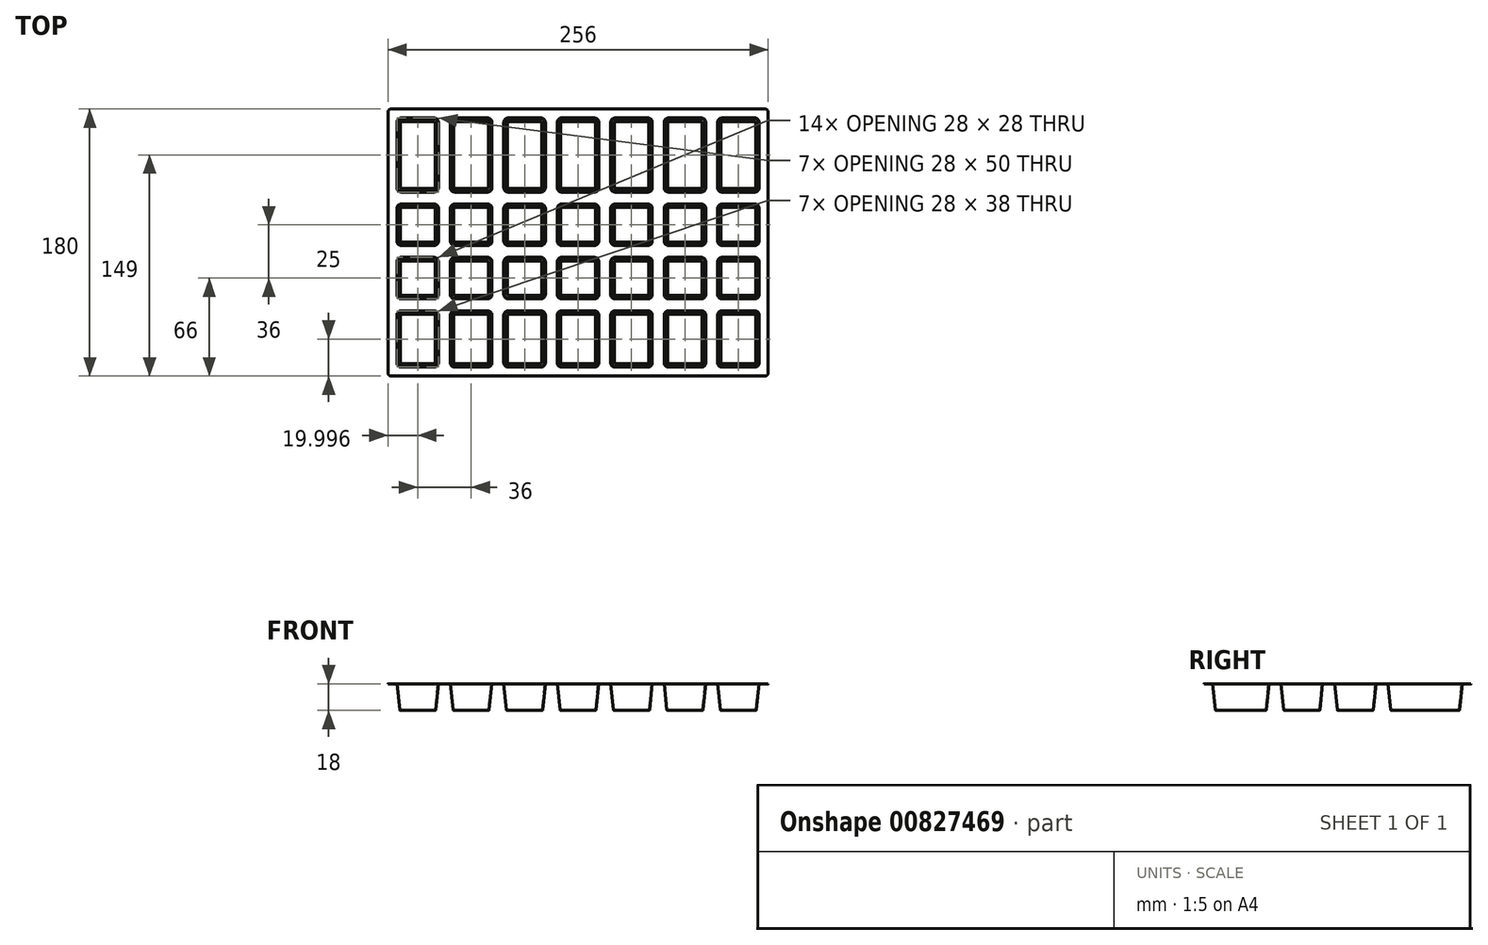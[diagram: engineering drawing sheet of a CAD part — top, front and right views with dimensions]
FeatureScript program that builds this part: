
annotation { "Feature Type Name" : "Feature", "Feature Type Description" : "" }
export const myFeature = defineFeature(function(context is Context, id is Id, definition is map)
    precondition{}
    {
        {
            var Q0;
            Q0=qCreatedBy(makeId("Top.planeOp"),FACE);
            var sketch = newSketch(context, id + "F0", { "sketchPlane" : qUnion([Q0])});
            skLineSegment(sketch, "E0.bottom", {"start": v(4.65, 0) * mm, "end": v(4.65, -180) * mm, "construction": true});
            skLineSegment(sketch, "E0.top", {"start": v(260.65, 0) * mm, "end": v(260.65, -180) * mm, "construction": true});
            skLineSegment(sketch, "E0.left", {"start": v(4.65, 0) * mm, "end": v(260.65, 0) * mm, "construction": true});
            skLineSegment(sketch, "E0.right", {"start": v(4.65, -180) * mm, "end": v(260.65, -180) * mm, "construction": true});
            skLineSegment(sketch, "E1", {"start": v(132.65, 0) * mm, "end": v(132.65, -180) * mm, "construction": true});
            skLineSegment(sketch, "E2.bottom", {"start": v(118.65, -9) * mm, "end": v(118.65, -53) * mm});
            skLineSegment(sketch, "E2.top", {"start": v(146.65, -9) * mm, "end": v(146.65, -53) * mm});
            skLineSegment(sketch, "E2.left", {"start": v(143.65, -6) * mm, "end": v(121.65, -6) * mm});
            skLineSegment(sketch, "E2.right", {"start": v(143.65, -56) * mm, "end": v(121.65, -56) * mm});
            skPoint(sketch, "E3", {"position": v(132.65, -6) * mm});
            skPoint(sketch, "E4.visualSharp", {"position": v(146.65, -6) * mm});
            skArc(sketch, "E4.filletArc", {"start": v(146.65, -9) * mm, "mid": v(145.77, -6.88) * mm, "end": v(143.65, -6) * mm});
            skPoint(sketch, "E5.visualSharp", {"position": v(118.65, -6) * mm});
            skArc(sketch, "E5.filletArc", {"start": v(121.65, -6) * mm, "mid": v(119.52, -6.88) * mm, "end": v(118.65, -9) * mm});
            skPoint(sketch, "E6.visualSharp", {"position": v(118.65, -56) * mm});
            skArc(sketch, "E6.filletArc", {"start": v(118.65, -53) * mm, "mid": v(119.52, -55.12) * mm, "end": v(121.65, -56) * mm});
            skPoint(sketch, "E7.visualSharp", {"position": v(146.65, -56) * mm});
            skArc(sketch, "E7.filletArc", {"start": v(143.65, -56) * mm, "mid": v(145.77, -55.12) * mm, "end": v(146.65, -53) * mm});
            skLineSegment(sketch, "E8.bottom", {"start": v(146.65, -67) * mm, "end": v(146.65, -89) * mm});
            skLineSegment(sketch, "E8.top", {"start": v(118.65, -67) * mm, "end": v(118.65, -89) * mm});
            skLineSegment(sketch, "E8.left", {"start": v(143.65, -64) * mm, "end": v(121.65, -64) * mm});
            skLineSegment(sketch, "E8.right", {"start": v(143.65, -92) * mm, "end": v(121.65, -92) * mm});
            skLineSegment(sketch, "E9.bottom", {"start": v(146.65, -103) * mm, "end": v(146.65, -125) * mm});
            skLineSegment(sketch, "E9.top", {"start": v(118.65, -103) * mm, "end": v(118.65, -125) * mm});
            skLineSegment(sketch, "E9.left", {"start": v(143.65, -100) * mm, "end": v(121.65, -100) * mm});
            skLineSegment(sketch, "E9.right", {"start": v(143.65, -128) * mm, "end": v(121.65, -128) * mm});
            skLineSegment(sketch, "E10.bottom", {"start": v(146.65, -139) * mm, "end": v(146.65, -171) * mm});
            skLineSegment(sketch, "E10.top", {"start": v(118.65, -139) * mm, "end": v(118.65, -171) * mm});
            skLineSegment(sketch, "E10.left", {"start": v(143.65, -136) * mm, "end": v(121.65, -136) * mm});
            skLineSegment(sketch, "E10.right", {"start": v(143.65, -174) * mm, "end": v(121.65, -174) * mm});
            skPoint(sketch, "E11.visualSharp", {"position": v(146.65, -64) * mm});
            skArc(sketch, "E11.filletArc", {"start": v(146.65, -67) * mm, "mid": v(145.77, -64.88) * mm, "end": v(143.65, -64) * mm});
            skPoint(sketch, "E12.visualSharp", {"position": v(146.65, -92) * mm});
            skArc(sketch, "E12.filletArc", {"start": v(143.65, -92) * mm, "mid": v(145.77, -91.12) * mm, "end": v(146.65, -89) * mm});
            skPoint(sketch, "E13.visualSharp", {"position": v(118.65, -92) * mm});
            skArc(sketch, "E13.filletArc", {"start": v(118.65, -89) * mm, "mid": v(119.52, -91.12) * mm, "end": v(121.65, -92) * mm});
            skPoint(sketch, "E14.visualSharp", {"position": v(118.65, -64) * mm});
            skArc(sketch, "E14.filletArc", {"start": v(121.65, -64) * mm, "mid": v(119.52, -64.88) * mm, "end": v(118.65, -67) * mm});
            skPoint(sketch, "E15.visualSharp", {"position": v(146.65, -100) * mm});
            skArc(sketch, "E15.filletArc", {"start": v(146.65, -103) * mm, "mid": v(145.77, -100.88) * mm, "end": v(143.65, -100) * mm});
            skPoint(sketch, "E16.visualSharp", {"position": v(146.65, -128) * mm});
            skArc(sketch, "E16.filletArc", {"start": v(143.65, -128) * mm, "mid": v(145.77, -127.12) * mm, "end": v(146.65, -125) * mm});
            skPoint(sketch, "E17.visualSharp", {"position": v(118.65, -128) * mm});
            skArc(sketch, "E17.filletArc", {"start": v(118.65, -125) * mm, "mid": v(119.52, -127.12) * mm, "end": v(121.65, -128) * mm});
            skPoint(sketch, "E18.visualSharp", {"position": v(118.65, -100) * mm});
            skArc(sketch, "E18.filletArc", {"start": v(121.65, -100) * mm, "mid": v(119.52, -100.88) * mm, "end": v(118.65, -103) * mm});
            skPoint(sketch, "E19.visualSharp", {"position": v(146.65, -136) * mm});
            skArc(sketch, "E19.filletArc", {"start": v(146.65, -139) * mm, "mid": v(145.77, -136.88) * mm, "end": v(143.65, -136) * mm});
            skPoint(sketch, "E20.visualSharp", {"position": v(146.65, -174) * mm});
            skArc(sketch, "E20.filletArc", {"start": v(143.65, -174) * mm, "mid": v(145.77, -173.12) * mm, "end": v(146.65, -171) * mm});
            skPoint(sketch, "E21.visualSharp", {"position": v(118.65, -174) * mm});
            skArc(sketch, "E21.filletArc", {"start": v(118.65, -171) * mm, "mid": v(119.52, -173.12) * mm, "end": v(121.65, -174) * mm});
            skPoint(sketch, "E22.visualSharp", {"position": v(118.65, -136) * mm});
            skArc(sketch, "E22.filletArc", {"start": v(121.65, -136) * mm, "mid": v(119.52, -136.88) * mm, "end": v(118.65, -139) * mm});
            skPoint(sketch, "E23.0.1.0", {"position": v(154.65, -56) * mm});
            skPoint(sketch, "E23.0.1.1", {"position": v(182.65, -56) * mm});
            skLineSegment(sketch, "E23.0.1.2", {"start": v(168.65, 0) * mm, "end": v(168.65, -180) * mm, "construction": true});
            skPoint(sketch, "E23.0.1.3", {"position": v(154.65, -6) * mm});
            skLineSegment(sketch, "E23.0.1.4", {"start": v(154.65, -9) * mm, "end": v(154.65, -53) * mm});
            skPoint(sketch, "E23.0.1.5", {"position": v(168.65, -6) * mm});
            skPoint(sketch, "E23.0.1.6", {"position": v(182.65, -174) * mm});
            skLineSegment(sketch, "E23.0.1.7", {"start": v(182.65, -67) * mm, "end": v(182.65, -89) * mm});
            skLineSegment(sketch, "E23.0.1.8", {"start": v(182.65, -9) * mm, "end": v(182.65, -53) * mm});
            skPoint(sketch, "E23.0.1.9", {"position": v(182.65, -64) * mm});
            skPoint(sketch, "E23.0.1.10", {"position": v(154.65, -174) * mm});
            skLineSegment(sketch, "E23.0.1.11", {"start": v(179.65, -64) * mm, "end": v(157.65, -64) * mm});
            skLineSegment(sketch, "E23.0.1.12", {"start": v(154.65, -139) * mm, "end": v(154.65, -171) * mm});
            skLineSegment(sketch, "E23.0.1.13", {"start": v(182.65, -103) * mm, "end": v(182.65, -125) * mm});
            skLineSegment(sketch, "E23.0.1.14", {"start": v(154.65, -103) * mm, "end": v(154.65, -125) * mm});
            skLineSegment(sketch, "E23.0.1.15", {"start": v(179.65, -174) * mm, "end": v(157.65, -174) * mm});
            skLineSegment(sketch, "E23.0.1.16", {"start": v(179.65, -92) * mm, "end": v(157.65, -92) * mm});
            skLineSegment(sketch, "E23.0.1.17", {"start": v(179.65, -56) * mm, "end": v(157.65, -56) * mm});
            skPoint(sketch, "E23.0.1.18", {"position": v(154.65, -92) * mm});
            skLineSegment(sketch, "E23.0.1.19", {"start": v(154.65, -67) * mm, "end": v(154.65, -89) * mm});
            skPoint(sketch, "E23.0.1.20", {"position": v(182.65, -128) * mm});
            skPoint(sketch, "E23.0.1.21", {"position": v(182.65, -136) * mm});
            skLineSegment(sketch, "E23.0.1.22", {"start": v(179.65, -100) * mm, "end": v(157.65, -100) * mm});
            skPoint(sketch, "E23.0.1.23", {"position": v(182.65, -100) * mm});
            skPoint(sketch, "E23.0.1.24", {"position": v(154.65, -64) * mm});
            skPoint(sketch, "E23.0.1.25", {"position": v(154.65, -128) * mm});
            skLineSegment(sketch, "E23.0.1.26", {"start": v(179.65, -128) * mm, "end": v(157.65, -128) * mm});
            skPoint(sketch, "E23.0.1.27", {"position": v(154.65, -100) * mm});
            skLineSegment(sketch, "E23.0.1.28", {"start": v(182.65, -139) * mm, "end": v(182.65, -171) * mm});
            skPoint(sketch, "E23.0.1.29", {"position": v(182.65, -92) * mm});
            skLineSegment(sketch, "E23.0.1.30", {"start": v(179.65, -6) * mm, "end": v(157.65, -6) * mm});
            skPoint(sketch, "E23.0.1.31", {"position": v(182.65, -6) * mm});
            skPoint(sketch, "E23.0.1.32", {"position": v(154.65, -136) * mm});
            skLineSegment(sketch, "E23.0.1.33", {"start": v(179.65, -136) * mm, "end": v(157.65, -136) * mm});
            skArc(sketch, "E23.0.1.34", {"start": v(154.65, -89) * mm, "mid": v(155.52, -91.12) * mm, "end": v(157.65, -92) * mm});
            skArc(sketch, "E23.0.1.35", {"start": v(154.65, -53) * mm, "mid": v(155.52, -55.12) * mm, "end": v(157.65, -56) * mm});
            skArc(sketch, "E23.0.1.36", {"start": v(182.65, -139) * mm, "mid": v(181.77, -136.88) * mm, "end": v(179.65, -136) * mm});
            skArc(sketch, "E23.0.1.37", {"start": v(157.65, -64) * mm, "mid": v(155.52, -64.88) * mm, "end": v(154.65, -67) * mm});
            skArc(sketch, "E23.0.1.38", {"start": v(179.65, -56) * mm, "mid": v(181.77, -55.12) * mm, "end": v(182.65, -53) * mm});
            skArc(sketch, "E23.0.1.39", {"start": v(154.65, -171) * mm, "mid": v(155.52, -173.12) * mm, "end": v(157.65, -174) * mm});
            skArc(sketch, "E23.0.1.40", {"start": v(157.65, -6) * mm, "mid": v(155.52, -6.88) * mm, "end": v(154.65, -9) * mm});
            skArc(sketch, "E23.0.1.41", {"start": v(157.65, -136) * mm, "mid": v(155.52, -136.88) * mm, "end": v(154.65, -139) * mm});
            skArc(sketch, "E23.0.1.42", {"start": v(157.65, -100) * mm, "mid": v(155.52, -100.88) * mm, "end": v(154.65, -103) * mm});
            skArc(sketch, "E23.0.1.43", {"start": v(182.65, -67) * mm, "mid": v(181.77, -64.88) * mm, "end": v(179.65, -64) * mm});
            skArc(sketch, "E23.0.1.44", {"start": v(154.65, -125) * mm, "mid": v(155.52, -127.12) * mm, "end": v(157.65, -128) * mm});
            skArc(sketch, "E23.0.1.45", {"start": v(179.65, -128) * mm, "mid": v(181.77, -127.12) * mm, "end": v(182.65, -125) * mm});
            skArc(sketch, "E23.0.1.46", {"start": v(179.65, -92) * mm, "mid": v(181.77, -91.12) * mm, "end": v(182.65, -89) * mm});
            skArc(sketch, "E23.0.1.47", {"start": v(182.65, -103) * mm, "mid": v(181.77, -100.88) * mm, "end": v(179.65, -100) * mm});
            skArc(sketch, "E23.0.1.48", {"start": v(179.65, -174) * mm, "mid": v(181.77, -173.12) * mm, "end": v(182.65, -171) * mm});
            skArc(sketch, "E23.0.1.49", {"start": v(182.65, -9) * mm, "mid": v(181.77, -6.88) * mm, "end": v(179.65, -6) * mm});
            skPoint(sketch, "E23.0.2.0", {"position": v(190.65, -56) * mm});
            skPoint(sketch, "E23.0.2.1", {"position": v(218.65, -56) * mm});
            skLineSegment(sketch, "E23.0.2.2", {"start": v(204.65, 0) * mm, "end": v(204.65, -180) * mm, "construction": true});
            skPoint(sketch, "E23.0.2.3", {"position": v(190.65, -6) * mm});
            skLineSegment(sketch, "E23.0.2.4", {"start": v(190.65, -9) * mm, "end": v(190.65, -53) * mm});
            skPoint(sketch, "E23.0.2.5", {"position": v(204.65, -6) * mm});
            skPoint(sketch, "E23.0.2.6", {"position": v(218.65, -174) * mm});
            skLineSegment(sketch, "E23.0.2.7", {"start": v(218.65, -67) * mm, "end": v(218.65, -89) * mm});
            skLineSegment(sketch, "E23.0.2.8", {"start": v(218.65, -9) * mm, "end": v(218.65, -53) * mm});
            skPoint(sketch, "E23.0.2.9", {"position": v(218.65, -64) * mm});
            skPoint(sketch, "E23.0.2.10", {"position": v(190.65, -174) * mm});
            skLineSegment(sketch, "E23.0.2.11", {"start": v(215.65, -64) * mm, "end": v(193.65, -64) * mm});
            skLineSegment(sketch, "E23.0.2.12", {"start": v(190.65, -139) * mm, "end": v(190.65, -171) * mm});
            skLineSegment(sketch, "E23.0.2.13", {"start": v(218.65, -103) * mm, "end": v(218.65, -125) * mm});
            skLineSegment(sketch, "E23.0.2.14", {"start": v(190.65, -103) * mm, "end": v(190.65, -125) * mm});
            skLineSegment(sketch, "E23.0.2.15", {"start": v(215.65, -174) * mm, "end": v(193.65, -174) * mm});
            skLineSegment(sketch, "E23.0.2.16", {"start": v(215.65, -92) * mm, "end": v(193.65, -92) * mm});
            skLineSegment(sketch, "E23.0.2.17", {"start": v(215.65, -56) * mm, "end": v(193.65, -56) * mm});
            skPoint(sketch, "E23.0.2.18", {"position": v(190.65, -92) * mm});
            skLineSegment(sketch, "E23.0.2.19", {"start": v(190.65, -67) * mm, "end": v(190.65, -89) * mm});
            skPoint(sketch, "E23.0.2.20", {"position": v(218.65, -128) * mm});
            skPoint(sketch, "E23.0.2.21", {"position": v(218.65, -136) * mm});
            skLineSegment(sketch, "E23.0.2.22", {"start": v(215.65, -100) * mm, "end": v(193.65, -100) * mm});
            skPoint(sketch, "E23.0.2.23", {"position": v(218.65, -100) * mm});
            skPoint(sketch, "E23.0.2.24", {"position": v(190.65, -64) * mm});
            skPoint(sketch, "E23.0.2.25", {"position": v(190.65, -128) * mm});
            skLineSegment(sketch, "E23.0.2.26", {"start": v(215.65, -128) * mm, "end": v(193.65, -128) * mm});
            skPoint(sketch, "E23.0.2.27", {"position": v(190.65, -100) * mm});
            skLineSegment(sketch, "E23.0.2.28", {"start": v(218.65, -139) * mm, "end": v(218.65, -171) * mm});
            skPoint(sketch, "E23.0.2.29", {"position": v(218.65, -92) * mm});
            skLineSegment(sketch, "E23.0.2.30", {"start": v(215.65, -6) * mm, "end": v(193.65, -6) * mm});
            skPoint(sketch, "E23.0.2.31", {"position": v(218.65, -6) * mm});
            skPoint(sketch, "E23.0.2.32", {"position": v(190.65, -136) * mm});
            skLineSegment(sketch, "E23.0.2.33", {"start": v(215.65, -136) * mm, "end": v(193.65, -136) * mm});
            skArc(sketch, "E23.0.2.34", {"start": v(190.65, -89) * mm, "mid": v(191.52, -91.12) * mm, "end": v(193.65, -92) * mm});
            skArc(sketch, "E23.0.2.35", {"start": v(190.65, -53) * mm, "mid": v(191.52, -55.12) * mm, "end": v(193.65, -56) * mm});
            skArc(sketch, "E23.0.2.36", {"start": v(218.65, -139) * mm, "mid": v(217.77, -136.88) * mm, "end": v(215.65, -136) * mm});
            skArc(sketch, "E23.0.2.37", {"start": v(193.65, -64) * mm, "mid": v(191.52, -64.88) * mm, "end": v(190.65, -67) * mm});
            skArc(sketch, "E23.0.2.38", {"start": v(215.65, -56) * mm, "mid": v(217.77, -55.12) * mm, "end": v(218.65, -53) * mm});
            skArc(sketch, "E23.0.2.39", {"start": v(190.65, -171) * mm, "mid": v(191.52, -173.12) * mm, "end": v(193.65, -174) * mm});
            skArc(sketch, "E23.0.2.40", {"start": v(193.65, -6) * mm, "mid": v(191.52, -6.88) * mm, "end": v(190.65, -9) * mm});
            skArc(sketch, "E23.0.2.41", {"start": v(193.65, -136) * mm, "mid": v(191.52, -136.88) * mm, "end": v(190.65, -139) * mm});
            skArc(sketch, "E23.0.2.42", {"start": v(193.65, -100) * mm, "mid": v(191.52, -100.88) * mm, "end": v(190.65, -103) * mm});
            skArc(sketch, "E23.0.2.43", {"start": v(218.65, -67) * mm, "mid": v(217.77, -64.88) * mm, "end": v(215.65, -64) * mm});
            skArc(sketch, "E23.0.2.44", {"start": v(190.65, -125) * mm, "mid": v(191.52, -127.12) * mm, "end": v(193.65, -128) * mm});
            skArc(sketch, "E23.0.2.45", {"start": v(215.65, -128) * mm, "mid": v(217.77, -127.12) * mm, "end": v(218.65, -125) * mm});
            skArc(sketch, "E23.0.2.46", {"start": v(215.65, -92) * mm, "mid": v(217.77, -91.12) * mm, "end": v(218.65, -89) * mm});
            skArc(sketch, "E23.0.2.47", {"start": v(218.65, -103) * mm, "mid": v(217.77, -100.88) * mm, "end": v(215.65, -100) * mm});
            skArc(sketch, "E23.0.2.48", {"start": v(215.65, -174) * mm, "mid": v(217.77, -173.12) * mm, "end": v(218.65, -171) * mm});
            skArc(sketch, "E23.0.2.49", {"start": v(218.65, -9) * mm, "mid": v(217.77, -6.88) * mm, "end": v(215.65, -6) * mm});
            skPoint(sketch, "E23.0.3.0", {"position": v(226.65, -56) * mm});
            skPoint(sketch, "E23.0.3.1", {"position": v(254.65, -56) * mm});
            skLineSegment(sketch, "E23.0.3.2", {"start": v(240.65, 0) * mm, "end": v(240.65, -180) * mm, "construction": true});
            skPoint(sketch, "E23.0.3.3", {"position": v(226.65, -6) * mm});
            skLineSegment(sketch, "E23.0.3.4", {"start": v(226.65, -9) * mm, "end": v(226.65, -53) * mm});
            skPoint(sketch, "E23.0.3.5", {"position": v(240.65, -6) * mm});
            skPoint(sketch, "E23.0.3.6", {"position": v(254.65, -174) * mm});
            skLineSegment(sketch, "E23.0.3.7", {"start": v(254.65, -67) * mm, "end": v(254.65, -89) * mm});
            skLineSegment(sketch, "E23.0.3.8", {"start": v(254.65, -9) * mm, "end": v(254.65, -53) * mm});
            skPoint(sketch, "E23.0.3.9", {"position": v(254.65, -64) * mm});
            skPoint(sketch, "E23.0.3.10", {"position": v(226.65, -174) * mm});
            skLineSegment(sketch, "E23.0.3.11", {"start": v(251.65, -64) * mm, "end": v(229.65, -64) * mm});
            skLineSegment(sketch, "E23.0.3.12", {"start": v(226.65, -139) * mm, "end": v(226.65, -171) * mm});
            skLineSegment(sketch, "E23.0.3.13", {"start": v(254.65, -103) * mm, "end": v(254.65, -125) * mm});
            skLineSegment(sketch, "E23.0.3.14", {"start": v(226.65, -103) * mm, "end": v(226.65, -125) * mm});
            skLineSegment(sketch, "E23.0.3.15", {"start": v(251.65, -174) * mm, "end": v(229.65, -174) * mm});
            skLineSegment(sketch, "E23.0.3.16", {"start": v(251.65, -92) * mm, "end": v(229.65, -92) * mm});
            skLineSegment(sketch, "E23.0.3.17", {"start": v(251.65, -56) * mm, "end": v(229.65, -56) * mm});
            skPoint(sketch, "E23.0.3.18", {"position": v(226.65, -92) * mm});
            skLineSegment(sketch, "E23.0.3.19", {"start": v(226.65, -67) * mm, "end": v(226.65, -89) * mm});
            skPoint(sketch, "E23.0.3.20", {"position": v(254.65, -128) * mm});
            skPoint(sketch, "E23.0.3.21", {"position": v(254.65, -136) * mm});
            skLineSegment(sketch, "E23.0.3.22", {"start": v(251.65, -100) * mm, "end": v(229.65, -100) * mm});
            skPoint(sketch, "E23.0.3.23", {"position": v(254.65, -100) * mm});
            skPoint(sketch, "E23.0.3.24", {"position": v(226.65, -64) * mm});
            skPoint(sketch, "E23.0.3.25", {"position": v(226.65, -128) * mm});
            skLineSegment(sketch, "E23.0.3.26", {"start": v(251.65, -128) * mm, "end": v(229.65, -128) * mm});
            skPoint(sketch, "E23.0.3.27", {"position": v(226.65, -100) * mm});
            skLineSegment(sketch, "E23.0.3.28", {"start": v(254.65, -139) * mm, "end": v(254.65, -171) * mm});
            skPoint(sketch, "E23.0.3.29", {"position": v(254.65, -92) * mm});
            skLineSegment(sketch, "E23.0.3.30", {"start": v(251.65, -6) * mm, "end": v(229.65, -6) * mm});
            skPoint(sketch, "E23.0.3.31", {"position": v(254.65, -6) * mm});
            skPoint(sketch, "E23.0.3.32", {"position": v(226.65, -136) * mm});
            skLineSegment(sketch, "E23.0.3.33", {"start": v(251.65, -136) * mm, "end": v(229.65, -136) * mm});
            skArc(sketch, "E23.0.3.34", {"start": v(226.65, -89) * mm, "mid": v(227.52, -91.12) * mm, "end": v(229.65, -92) * mm});
            skArc(sketch, "E23.0.3.35", {"start": v(226.65, -53) * mm, "mid": v(227.52, -55.12) * mm, "end": v(229.65, -56) * mm});
            skArc(sketch, "E23.0.3.36", {"start": v(254.65, -139) * mm, "mid": v(253.77, -136.88) * mm, "end": v(251.65, -136) * mm});
            skArc(sketch, "E23.0.3.37", {"start": v(229.65, -64) * mm, "mid": v(227.52, -64.88) * mm, "end": v(226.65, -67) * mm});
            skArc(sketch, "E23.0.3.38", {"start": v(251.65, -56) * mm, "mid": v(253.77, -55.12) * mm, "end": v(254.65, -53) * mm});
            skArc(sketch, "E23.0.3.39", {"start": v(226.65, -171) * mm, "mid": v(227.52, -173.12) * mm, "end": v(229.65, -174) * mm});
            skArc(sketch, "E23.0.3.40", {"start": v(229.65, -6) * mm, "mid": v(227.52, -6.88) * mm, "end": v(226.65, -9) * mm});
            skArc(sketch, "E23.0.3.41", {"start": v(229.65, -136) * mm, "mid": v(227.52, -136.88) * mm, "end": v(226.65, -139) * mm});
            skArc(sketch, "E23.0.3.42", {"start": v(229.65, -100) * mm, "mid": v(227.52, -100.88) * mm, "end": v(226.65, -103) * mm});
            skArc(sketch, "E23.0.3.43", {"start": v(254.65, -67) * mm, "mid": v(253.77, -64.88) * mm, "end": v(251.65, -64) * mm});
            skArc(sketch, "E23.0.3.44", {"start": v(226.65, -125) * mm, "mid": v(227.52, -127.12) * mm, "end": v(229.65, -128) * mm});
            skArc(sketch, "E23.0.3.45", {"start": v(251.65, -128) * mm, "mid": v(253.77, -127.12) * mm, "end": v(254.65, -125) * mm});
            skArc(sketch, "E23.0.3.46", {"start": v(251.65, -92) * mm, "mid": v(253.77, -91.12) * mm, "end": v(254.65, -89) * mm});
            skArc(sketch, "E23.0.3.47", {"start": v(254.65, -103) * mm, "mid": v(253.77, -100.88) * mm, "end": v(251.65, -100) * mm});
            skArc(sketch, "E23.0.3.48", {"start": v(251.65, -174) * mm, "mid": v(253.77, -173.12) * mm, "end": v(254.65, -171) * mm});
            skArc(sketch, "E23.0.3.49", {"start": v(254.65, -9) * mm, "mid": v(253.77, -6.88) * mm, "end": v(251.65, -6) * mm});
            skLineSegment(sketch, "E23.direction1", {"start": v(132.65, -6) * mm, "end": v(132.65, -31.13) * mm, "construction": true});
            skLineSegment(sketch, "E23.direction2", {"start": v(132.65, -6) * mm, "end": v(168.65, -6) * mm, "construction": true});
            skLineSegment(sketch, "E24.0.1.0", {"start": v(107.65, -92) * mm, "end": v(85.65, -92) * mm});
            skLineSegment(sketch, "E24.0.1.1", {"start": v(107.65, -128) * mm, "end": v(85.65, -128) * mm});
            skPoint(sketch, "E24.0.1.2", {"position": v(96.65, -6) * mm});
            skLineSegment(sketch, "E24.0.1.3", {"start": v(82.65, -139) * mm, "end": v(82.65, -171) * mm});
            skPoint(sketch, "E24.0.1.4", {"position": v(82.65, -100) * mm});
            skPoint(sketch, "E24.0.1.5", {"position": v(110.65, -6) * mm});
            skLineSegment(sketch, "E24.0.1.6", {"start": v(107.65, -100) * mm, "end": v(85.65, -100) * mm});
            skPoint(sketch, "E24.0.1.7", {"position": v(110.65, -174) * mm});
            skPoint(sketch, "E24.0.1.8", {"position": v(110.65, -56) * mm});
            skPoint(sketch, "E24.0.1.9", {"position": v(110.65, -100) * mm});
            skPoint(sketch, "E24.0.1.10", {"position": v(110.65, -64) * mm});
            skLineSegment(sketch, "E24.0.1.11", {"start": v(107.65, -174) * mm, "end": v(85.65, -174) * mm});
            skPoint(sketch, "E24.0.1.12", {"position": v(82.65, -92) * mm});
            skPoint(sketch, "E24.0.1.13", {"position": v(110.65, -92) * mm});
            skPoint(sketch, "E24.0.1.14", {"position": v(82.65, -136) * mm});
            skPoint(sketch, "E24.0.1.15", {"position": v(82.65, -56) * mm});
            skLineSegment(sketch, "E24.0.1.16", {"start": v(110.65, -9) * mm, "end": v(110.65, -53) * mm});
            skLineSegment(sketch, "E24.0.1.17", {"start": v(82.65, -103) * mm, "end": v(82.65, -125) * mm});
            skLineSegment(sketch, "E24.0.1.18", {"start": v(110.65, -103) * mm, "end": v(110.65, -125) * mm});
            skPoint(sketch, "E24.0.1.19", {"position": v(82.65, -174) * mm});
            skPoint(sketch, "E24.0.1.20", {"position": v(110.65, -136) * mm});
            skPoint(sketch, "E24.0.1.21", {"position": v(82.65, -6) * mm});
            skPoint(sketch, "E24.0.1.22", {"position": v(110.65, -128) * mm});
            skPoint(sketch, "E24.0.1.23", {"position": v(82.65, -64) * mm});
            skLineSegment(sketch, "E24.0.1.24", {"start": v(82.65, -67) * mm, "end": v(82.65, -89) * mm});
            skLineSegment(sketch, "E24.0.1.25", {"start": v(107.65, -64) * mm, "end": v(85.65, -64) * mm});
            skLineSegment(sketch, "E24.0.1.26", {"start": v(110.65, -139) * mm, "end": v(110.65, -171) * mm});
            skLineSegment(sketch, "E24.0.1.27", {"start": v(110.65, -67) * mm, "end": v(110.65, -89) * mm});
            skLineSegment(sketch, "E24.0.1.28", {"start": v(82.65, -9) * mm, "end": v(82.65, -53) * mm});
            skPoint(sketch, "E24.0.1.29", {"position": v(82.65, -128) * mm});
            skLineSegment(sketch, "E24.0.1.30", {"start": v(96.65, 0) * mm, "end": v(96.65, -180) * mm, "construction": true});
            skLineSegment(sketch, "E24.0.1.31", {"start": v(107.65, -56) * mm, "end": v(85.65, -56) * mm});
            skLineSegment(sketch, "E24.0.1.32", {"start": v(107.65, -136) * mm, "end": v(85.65, -136) * mm});
            skLineSegment(sketch, "E24.0.1.33", {"start": v(107.65, -6) * mm, "end": v(85.65, -6) * mm});
            skLineSegment(sketch, "E24.0.1.34", {"start": v(96.65, -6) * mm, "end": v(96.65, -31.13) * mm, "construction": true});
            skArc(sketch, "E24.0.1.35", {"start": v(82.65, -171) * mm, "mid": v(83.52, -173.12) * mm, "end": v(85.65, -174) * mm});
            skArc(sketch, "E24.0.1.36", {"start": v(85.65, -6) * mm, "mid": v(83.52, -6.88) * mm, "end": v(82.65, -9) * mm});
            skArc(sketch, "E24.0.1.37", {"start": v(82.65, -89) * mm, "mid": v(83.52, -91.12) * mm, "end": v(85.65, -92) * mm});
            skArc(sketch, "E24.0.1.38", {"start": v(85.65, -64) * mm, "mid": v(83.52, -64.88) * mm, "end": v(82.65, -67) * mm});
            skArc(sketch, "E24.0.1.39", {"start": v(107.65, -56) * mm, "mid": v(109.77, -55.12) * mm, "end": v(110.65, -53) * mm});
            skArc(sketch, "E24.0.1.40", {"start": v(107.65, -128) * mm, "mid": v(109.77, -127.12) * mm, "end": v(110.65, -125) * mm});
            skArc(sketch, "E24.0.1.41", {"start": v(107.65, -92) * mm, "mid": v(109.77, -91.12) * mm, "end": v(110.65, -89) * mm});
            skArc(sketch, "E24.0.1.42", {"start": v(85.65, -136) * mm, "mid": v(83.52, -136.88) * mm, "end": v(82.65, -139) * mm});
            skArc(sketch, "E24.0.1.43", {"start": v(82.65, -125) * mm, "mid": v(83.52, -127.12) * mm, "end": v(85.65, -128) * mm});
            skArc(sketch, "E24.0.1.44", {"start": v(107.65, -174) * mm, "mid": v(109.77, -173.12) * mm, "end": v(110.65, -171) * mm});
            skArc(sketch, "E24.0.1.45", {"start": v(82.65, -53) * mm, "mid": v(83.52, -55.12) * mm, "end": v(85.65, -56) * mm});
            skArc(sketch, "E24.0.1.46", {"start": v(110.65, -9) * mm, "mid": v(109.77, -6.88) * mm, "end": v(107.65, -6) * mm});
            skArc(sketch, "E24.0.1.47", {"start": v(110.65, -103) * mm, "mid": v(109.77, -100.88) * mm, "end": v(107.65, -100) * mm});
            skArc(sketch, "E24.0.1.48", {"start": v(85.65, -100) * mm, "mid": v(83.52, -100.88) * mm, "end": v(82.65, -103) * mm});
            skArc(sketch, "E24.0.1.49", {"start": v(110.65, -67) * mm, "mid": v(109.77, -64.88) * mm, "end": v(107.65, -64) * mm});
            skArc(sketch, "E24.0.1.50", {"start": v(110.65, -139) * mm, "mid": v(109.77, -136.88) * mm, "end": v(107.65, -136) * mm});
            skLineSegment(sketch, "E24.0.2.0", {"start": v(71.65, -92) * mm, "end": v(49.65, -92) * mm});
            skLineSegment(sketch, "E24.0.2.1", {"start": v(71.65, -128) * mm, "end": v(49.65, -128) * mm});
            skPoint(sketch, "E24.0.2.2", {"position": v(60.65, -6) * mm});
            skLineSegment(sketch, "E24.0.2.3", {"start": v(46.65, -139) * mm, "end": v(46.65, -171) * mm});
            skPoint(sketch, "E24.0.2.4", {"position": v(46.65, -100) * mm});
            skPoint(sketch, "E24.0.2.5", {"position": v(74.65, -6) * mm});
            skLineSegment(sketch, "E24.0.2.6", {"start": v(71.65, -100) * mm, "end": v(49.65, -100) * mm});
            skPoint(sketch, "E24.0.2.7", {"position": v(74.65, -174) * mm});
            skPoint(sketch, "E24.0.2.8", {"position": v(74.65, -56) * mm});
            skPoint(sketch, "E24.0.2.9", {"position": v(74.65, -100) * mm});
            skPoint(sketch, "E24.0.2.10", {"position": v(74.65, -64) * mm});
            skLineSegment(sketch, "E24.0.2.11", {"start": v(71.65, -174) * mm, "end": v(49.65, -174) * mm});
            skPoint(sketch, "E24.0.2.12", {"position": v(46.65, -92) * mm});
            skPoint(sketch, "E24.0.2.13", {"position": v(74.65, -92) * mm});
            skPoint(sketch, "E24.0.2.14", {"position": v(46.65, -136) * mm});
            skPoint(sketch, "E24.0.2.15", {"position": v(46.65, -56) * mm});
            skLineSegment(sketch, "E24.0.2.16", {"start": v(74.65, -9) * mm, "end": v(74.65, -53) * mm});
            skLineSegment(sketch, "E24.0.2.17", {"start": v(46.65, -103) * mm, "end": v(46.65, -125) * mm});
            skLineSegment(sketch, "E24.0.2.18", {"start": v(74.65, -103) * mm, "end": v(74.65, -125) * mm});
            skPoint(sketch, "E24.0.2.19", {"position": v(46.65, -174) * mm});
            skPoint(sketch, "E24.0.2.20", {"position": v(74.65, -136) * mm});
            skPoint(sketch, "E24.0.2.21", {"position": v(46.65, -6) * mm});
            skPoint(sketch, "E24.0.2.22", {"position": v(74.65, -128) * mm});
            skPoint(sketch, "E24.0.2.23", {"position": v(46.65, -64) * mm});
            skLineSegment(sketch, "E24.0.2.24", {"start": v(46.65, -67) * mm, "end": v(46.65, -89) * mm});
            skLineSegment(sketch, "E24.0.2.25", {"start": v(71.65, -64) * mm, "end": v(49.65, -64) * mm});
            skLineSegment(sketch, "E24.0.2.26", {"start": v(74.65, -139) * mm, "end": v(74.65, -171) * mm});
            skLineSegment(sketch, "E24.0.2.27", {"start": v(74.65, -67) * mm, "end": v(74.65, -89) * mm});
            skLineSegment(sketch, "E24.0.2.28", {"start": v(46.65, -9) * mm, "end": v(46.65, -53) * mm});
            skPoint(sketch, "E24.0.2.29", {"position": v(46.65, -128) * mm});
            skLineSegment(sketch, "E24.0.2.30", {"start": v(60.65, 0) * mm, "end": v(60.65, -180) * mm, "construction": true});
            skLineSegment(sketch, "E24.0.2.31", {"start": v(71.65, -56) * mm, "end": v(49.65, -56) * mm});
            skLineSegment(sketch, "E24.0.2.32", {"start": v(71.65, -136) * mm, "end": v(49.65, -136) * mm});
            skLineSegment(sketch, "E24.0.2.33", {"start": v(71.65, -6) * mm, "end": v(49.65, -6) * mm});
            skLineSegment(sketch, "E24.0.2.34", {"start": v(60.65, -6) * mm, "end": v(60.65, -31.13) * mm, "construction": true});
            skArc(sketch, "E24.0.2.35", {"start": v(46.65, -171) * mm, "mid": v(47.52, -173.12) * mm, "end": v(49.65, -174) * mm});
            skArc(sketch, "E24.0.2.36", {"start": v(49.65, -6) * mm, "mid": v(47.52, -6.88) * mm, "end": v(46.65, -9) * mm});
            skArc(sketch, "E24.0.2.37", {"start": v(46.65, -89) * mm, "mid": v(47.52, -91.12) * mm, "end": v(49.65, -92) * mm});
            skArc(sketch, "E24.0.2.38", {"start": v(49.65, -64) * mm, "mid": v(47.52, -64.88) * mm, "end": v(46.65, -67) * mm});
            skArc(sketch, "E24.0.2.39", {"start": v(71.65, -56) * mm, "mid": v(73.77, -55.12) * mm, "end": v(74.65, -53) * mm});
            skArc(sketch, "E24.0.2.40", {"start": v(71.65, -128) * mm, "mid": v(73.77, -127.12) * mm, "end": v(74.65, -125) * mm});
            skArc(sketch, "E24.0.2.41", {"start": v(71.65, -92) * mm, "mid": v(73.77, -91.12) * mm, "end": v(74.65, -89) * mm});
            skArc(sketch, "E24.0.2.42", {"start": v(49.65, -136) * mm, "mid": v(47.52, -136.88) * mm, "end": v(46.65, -139) * mm});
            skArc(sketch, "E24.0.2.43", {"start": v(46.65, -125) * mm, "mid": v(47.52, -127.12) * mm, "end": v(49.65, -128) * mm});
            skArc(sketch, "E24.0.2.44", {"start": v(71.65, -174) * mm, "mid": v(73.77, -173.12) * mm, "end": v(74.65, -171) * mm});
            skArc(sketch, "E24.0.2.45", {"start": v(46.65, -53) * mm, "mid": v(47.52, -55.12) * mm, "end": v(49.65, -56) * mm});
            skArc(sketch, "E24.0.2.46", {"start": v(74.65, -9) * mm, "mid": v(73.77, -6.88) * mm, "end": v(71.65, -6) * mm});
            skArc(sketch, "E24.0.2.47", {"start": v(74.65, -103) * mm, "mid": v(73.77, -100.88) * mm, "end": v(71.65, -100) * mm});
            skArc(sketch, "E24.0.2.48", {"start": v(49.65, -100) * mm, "mid": v(47.52, -100.88) * mm, "end": v(46.65, -103) * mm});
            skArc(sketch, "E24.0.2.49", {"start": v(74.65, -67) * mm, "mid": v(73.77, -64.88) * mm, "end": v(71.65, -64) * mm});
            skArc(sketch, "E24.0.2.50", {"start": v(74.65, -139) * mm, "mid": v(73.77, -136.88) * mm, "end": v(71.65, -136) * mm});
            skLineSegment(sketch, "E24.0.3.0", {"start": v(35.65, -92) * mm, "end": v(13.65, -92) * mm});
            skLineSegment(sketch, "E24.0.3.1", {"start": v(35.65, -128) * mm, "end": v(13.65, -128) * mm});
            skPoint(sketch, "E24.0.3.2", {"position": v(24.65, -6) * mm});
            skLineSegment(sketch, "E24.0.3.3", {"start": v(10.65, -139) * mm, "end": v(10.65, -171) * mm});
            skPoint(sketch, "E24.0.3.4", {"position": v(10.65, -100) * mm});
            skPoint(sketch, "E24.0.3.5", {"position": v(38.65, -6) * mm});
            skLineSegment(sketch, "E24.0.3.6", {"start": v(35.65, -100) * mm, "end": v(13.65, -100) * mm});
            skPoint(sketch, "E24.0.3.7", {"position": v(38.65, -174) * mm});
            skPoint(sketch, "E24.0.3.8", {"position": v(38.65, -56) * mm});
            skPoint(sketch, "E24.0.3.9", {"position": v(38.65, -100) * mm});
            skPoint(sketch, "E24.0.3.10", {"position": v(38.65, -64) * mm});
            skLineSegment(sketch, "E24.0.3.11", {"start": v(35.65, -174) * mm, "end": v(13.65, -174) * mm});
            skPoint(sketch, "E24.0.3.12", {"position": v(10.65, -92) * mm});
            skPoint(sketch, "E24.0.3.13", {"position": v(38.65, -92) * mm});
            skPoint(sketch, "E24.0.3.14", {"position": v(10.65, -136) * mm});
            skPoint(sketch, "E24.0.3.15", {"position": v(10.65, -56) * mm});
            skLineSegment(sketch, "E24.0.3.16", {"start": v(38.65, -9) * mm, "end": v(38.65, -53) * mm});
            skLineSegment(sketch, "E24.0.3.17", {"start": v(10.65, -103) * mm, "end": v(10.65, -125) * mm});
            skLineSegment(sketch, "E24.0.3.18", {"start": v(38.65, -103) * mm, "end": v(38.65, -125) * mm});
            skPoint(sketch, "E24.0.3.19", {"position": v(10.65, -174) * mm});
            skPoint(sketch, "E24.0.3.20", {"position": v(38.65, -136) * mm});
            skPoint(sketch, "E24.0.3.21", {"position": v(10.65, -6) * mm});
            skPoint(sketch, "E24.0.3.22", {"position": v(38.65, -128) * mm});
            skPoint(sketch, "E24.0.3.23", {"position": v(10.65, -64) * mm});
            skLineSegment(sketch, "E24.0.3.24", {"start": v(10.65, -67) * mm, "end": v(10.65, -89) * mm});
            skLineSegment(sketch, "E24.0.3.25", {"start": v(35.65, -64) * mm, "end": v(13.65, -64) * mm});
            skLineSegment(sketch, "E24.0.3.26", {"start": v(38.65, -139) * mm, "end": v(38.65, -171) * mm});
            skLineSegment(sketch, "E24.0.3.27", {"start": v(38.65, -67) * mm, "end": v(38.65, -89) * mm});
            skLineSegment(sketch, "E24.0.3.28", {"start": v(10.65, -9) * mm, "end": v(10.65, -53) * mm});
            skPoint(sketch, "E24.0.3.29", {"position": v(10.65, -128) * mm});
            skLineSegment(sketch, "E24.0.3.30", {"start": v(24.65, 0) * mm, "end": v(24.65, -180) * mm, "construction": true});
            skLineSegment(sketch, "E24.0.3.31", {"start": v(35.65, -56) * mm, "end": v(13.65, -56) * mm});
            skLineSegment(sketch, "E24.0.3.32", {"start": v(35.65, -136) * mm, "end": v(13.65, -136) * mm});
            skLineSegment(sketch, "E24.0.3.33", {"start": v(35.65, -6) * mm, "end": v(13.65, -6) * mm});
            skLineSegment(sketch, "E24.0.3.34", {"start": v(24.65, -6) * mm, "end": v(24.65, -31.13) * mm, "construction": true});
            skArc(sketch, "E24.0.3.35", {"start": v(10.65, -171) * mm, "mid": v(11.52, -173.12) * mm, "end": v(13.65, -174) * mm});
            skArc(sketch, "E24.0.3.36", {"start": v(13.65, -6) * mm, "mid": v(11.52, -6.88) * mm, "end": v(10.65, -9) * mm});
            skArc(sketch, "E24.0.3.37", {"start": v(10.65, -89) * mm, "mid": v(11.52, -91.12) * mm, "end": v(13.65, -92) * mm});
            skArc(sketch, "E24.0.3.38", {"start": v(13.65, -64) * mm, "mid": v(11.52, -64.88) * mm, "end": v(10.65, -67) * mm});
            skArc(sketch, "E24.0.3.39", {"start": v(35.65, -56) * mm, "mid": v(37.77, -55.12) * mm, "end": v(38.65, -53) * mm});
            skArc(sketch, "E24.0.3.40", {"start": v(35.65, -128) * mm, "mid": v(37.77, -127.12) * mm, "end": v(38.65, -125) * mm});
            skArc(sketch, "E24.0.3.41", {"start": v(35.65, -92) * mm, "mid": v(37.77, -91.12) * mm, "end": v(38.65, -89) * mm});
            skArc(sketch, "E24.0.3.42", {"start": v(13.65, -136) * mm, "mid": v(11.52, -136.88) * mm, "end": v(10.65, -139) * mm});
            skArc(sketch, "E24.0.3.43", {"start": v(10.65, -125) * mm, "mid": v(11.52, -127.12) * mm, "end": v(13.65, -128) * mm});
            skArc(sketch, "E24.0.3.44", {"start": v(35.65, -174) * mm, "mid": v(37.77, -173.12) * mm, "end": v(38.65, -171) * mm});
            skArc(sketch, "E24.0.3.45", {"start": v(10.65, -53) * mm, "mid": v(11.52, -55.12) * mm, "end": v(13.65, -56) * mm});
            skArc(sketch, "E24.0.3.46", {"start": v(38.65, -9) * mm, "mid": v(37.77, -6.88) * mm, "end": v(35.65, -6) * mm});
            skArc(sketch, "E24.0.3.47", {"start": v(38.65, -103) * mm, "mid": v(37.77, -100.88) * mm, "end": v(35.65, -100) * mm});
            skArc(sketch, "E24.0.3.48", {"start": v(13.65, -100) * mm, "mid": v(11.52, -100.88) * mm, "end": v(10.65, -103) * mm});
            skArc(sketch, "E24.0.3.49", {"start": v(38.65, -67) * mm, "mid": v(37.77, -64.88) * mm, "end": v(35.65, -64) * mm});
            skArc(sketch, "E24.0.3.50", {"start": v(38.65, -139) * mm, "mid": v(37.77, -136.88) * mm, "end": v(35.65, -136) * mm});
            skLineSegment(sketch, "E24.direction2", {"start": v(132.65, -6) * mm, "end": v(96.65, -6) * mm, "construction": true});
            skSolve(sketch);
        }
        {
            var Q0;
            Q0=qCreatedBy(makeId("Top.planeOp"),FACE);
            var sketch = newSketch(context, id + "F1", { "sketchPlane" : qUnion([Q0])});
            skLineSegment(sketch, "E25.bottom", {"start": v(4.65, 0) * mm, "end": v(260.65, 0) * mm});
            skLineSegment(sketch, "E25.top", {"start": v(4.65, -180) * mm, "end": v(260.65, -180) * mm});
            skLineSegment(sketch, "E25.left", {"start": v(4.65, -180) * mm, "end": v(4.65, 0) * mm});
            skLineSegment(sketch, "E25.right", {"start": v(260.65, -180) * mm, "end": v(260.65, 0) * mm});
            skSolve(sketch);
        }
        {
            var Q0;
            Q0 = qSketchRegion(id + "F1", true);
            extrude(context, id + "F2", {"entities" : qUnion([Q0]), "oppositeDirection" : true, "depth" : .1 * mm, "offsetDistance" : 25 * mm});
        }
        {
            var Q0;
            Q0 = qSketchRegion(id + "F0", true);
            extrude(context, id + "F3", {"entities" : qUnion([Q0]), "operationType" : NewBodyOperationType.REMOVE, "oppositeDirection" : true, "depth" : 25 * mm, "offsetDistance" : 25 * mm});
        }
        {
            var Q0;
            Q0 = qSketchRegion(id + "F0", true);
            extrude(context, id + "F4", {"entities" : qUnion([Q0]), "oppositeDirection" : true, "depth" : 18 * mm, "offsetDistance" : 25 * mm, "hasDraft" : true, "draftAngle" : 6 * degree, "draftPullDirection" : true});
        }
        {
            var Q0;
            Q0=makeQuery(id+"F4.opExtrude","CAP_FACE",FACE,{"disambiguationData":[OSD([sQuery(id+"F0.wireOp",EDGE,"E2.bottom"),sQuery(id+"F0.wireOp",EDGE,"E2.top"),sQuery(id+"F0.wireOp",EDGE,"E2.left"),sQuery(id+"F0.wireOp",EDGE,"E2.right"),sQuery(id+"F0.wireOp",EDGE,"E4.filletArc"),sQuery(id+"F0.wireOp",EDGE,"E5.filletArc"),sQuery(id+"F0.wireOp",EDGE,"E6.filletArc"),sQuery(id+"F0.wireOp",EDGE,"E7.filletArc")])],"isStart":true});
            var Q1;
            Q1=makeQuery(id+"F4.opExtrude","CAP_FACE",FACE,{"disambiguationData":[OSD([sQuery(id+"F0.wireOp",EDGE,"E8.bottom"),sQuery(id+"F0.wireOp",EDGE,"E8.top"),sQuery(id+"F0.wireOp",EDGE,"E8.left"),sQuery(id+"F0.wireOp",EDGE,"E8.right"),sQuery(id+"F0.wireOp",EDGE,"E11.filletArc"),sQuery(id+"F0.wireOp",EDGE,"E12.filletArc"),sQuery(id+"F0.wireOp",EDGE,"E13.filletArc"),sQuery(id+"F0.wireOp",EDGE,"E14.filletArc")])],"isStart":true});
            var Q2;
            Q2=makeQuery(id+"F4.opExtrude","CAP_FACE",FACE,{"disambiguationData":[OSD([sQuery(id+"F0.wireOp",EDGE,"E9.bottom"),sQuery(id+"F0.wireOp",EDGE,"E9.top"),sQuery(id+"F0.wireOp",EDGE,"E9.left"),sQuery(id+"F0.wireOp",EDGE,"E9.right"),sQuery(id+"F0.wireOp",EDGE,"E15.filletArc"),sQuery(id+"F0.wireOp",EDGE,"E16.filletArc"),sQuery(id+"F0.wireOp",EDGE,"E17.filletArc"),sQuery(id+"F0.wireOp",EDGE,"E18.filletArc")])],"isStart":true});
            var Q3;
            Q3=makeQuery(id+"F4.opExtrude","CAP_FACE",FACE,{"disambiguationData":[OSD([sQuery(id+"F0.wireOp",EDGE,"E10.bottom"),sQuery(id+"F0.wireOp",EDGE,"E10.top"),sQuery(id+"F0.wireOp",EDGE,"E10.left"),sQuery(id+"F0.wireOp",EDGE,"E10.right"),sQuery(id+"F0.wireOp",EDGE,"E19.filletArc"),sQuery(id+"F0.wireOp",EDGE,"E20.filletArc"),sQuery(id+"F0.wireOp",EDGE,"E21.filletArc"),sQuery(id+"F0.wireOp",EDGE,"E22.filletArc")])],"isStart":true});
            var Q4;
            Q4=makeQuery(id+"F4.opExtrude","CAP_FACE",FACE,{"disambiguationData":[OSD([sQuery(id+"F0.wireOp",EDGE,"E23.0.3.4"),sQuery(id+"F0.wireOp",EDGE,"E23.0.3.8"),sQuery(id+"F0.wireOp",EDGE,"E23.0.3.17"),sQuery(id+"F0.wireOp",EDGE,"E23.0.3.30"),sQuery(id+"F0.wireOp",EDGE,"E23.0.3.35"),sQuery(id+"F0.wireOp",EDGE,"E23.0.3.38"),sQuery(id+"F0.wireOp",EDGE,"E23.0.3.40"),sQuery(id+"F0.wireOp",EDGE,"E23.0.3.49")])],"isStart":true});
            var Q5;
            Q5=makeQuery(id+"F4.opExtrude","CAP_FACE",FACE,{"disambiguationData":[OSD([sQuery(id+"F0.wireOp",EDGE,"E23.0.3.7"),sQuery(id+"F0.wireOp",EDGE,"E23.0.3.11"),sQuery(id+"F0.wireOp",EDGE,"E23.0.3.16"),sQuery(id+"F0.wireOp",EDGE,"E23.0.3.19"),sQuery(id+"F0.wireOp",EDGE,"E23.0.3.34"),sQuery(id+"F0.wireOp",EDGE,"E23.0.3.37"),sQuery(id+"F0.wireOp",EDGE,"E23.0.3.43"),sQuery(id+"F0.wireOp",EDGE,"E23.0.3.46")])],"isStart":true});
            var Q6;
            Q6=makeQuery(id+"F4.opExtrude","CAP_FACE",FACE,{"disambiguationData":[OSD([sQuery(id+"F0.wireOp",EDGE,"E23.0.3.13"),sQuery(id+"F0.wireOp",EDGE,"E23.0.3.14"),sQuery(id+"F0.wireOp",EDGE,"E23.0.3.22"),sQuery(id+"F0.wireOp",EDGE,"E23.0.3.26"),sQuery(id+"F0.wireOp",EDGE,"E23.0.3.42"),sQuery(id+"F0.wireOp",EDGE,"E23.0.3.44"),sQuery(id+"F0.wireOp",EDGE,"E23.0.3.45"),sQuery(id+"F0.wireOp",EDGE,"E23.0.3.47")])],"isStart":true});
            var Q7;
            Q7=makeQuery(id+"F4.opExtrude","CAP_FACE",FACE,{"disambiguationData":[OSD([sQuery(id+"F0.wireOp",EDGE,"E23.0.3.12"),sQuery(id+"F0.wireOp",EDGE,"E23.0.3.15"),sQuery(id+"F0.wireOp",EDGE,"E23.0.3.28"),sQuery(id+"F0.wireOp",EDGE,"E23.0.3.33"),sQuery(id+"F0.wireOp",EDGE,"E23.0.3.36"),sQuery(id+"F0.wireOp",EDGE,"E23.0.3.39"),sQuery(id+"F0.wireOp",EDGE,"E23.0.3.41"),sQuery(id+"F0.wireOp",EDGE,"E23.0.3.48")])],"isStart":true});
            var Q8;
            Q8=makeQuery(id+"F4.opExtrude","CAP_FACE",FACE,{"disambiguationData":[OSD([sQuery(id+"F0.wireOp",EDGE,"E23.0.2.12"),sQuery(id+"F0.wireOp",EDGE,"E23.0.2.15"),sQuery(id+"F0.wireOp",EDGE,"E23.0.2.28"),sQuery(id+"F0.wireOp",EDGE,"E23.0.2.33"),sQuery(id+"F0.wireOp",EDGE,"E23.0.2.36"),sQuery(id+"F0.wireOp",EDGE,"E23.0.2.39"),sQuery(id+"F0.wireOp",EDGE,"E23.0.2.41"),sQuery(id+"F0.wireOp",EDGE,"E23.0.2.48")])],"isStart":true});
            var Q9;
            Q9=makeQuery(id+"F4.opExtrude","CAP_FACE",FACE,{"disambiguationData":[OSD([sQuery(id+"F0.wireOp",EDGE,"E23.0.2.13"),sQuery(id+"F0.wireOp",EDGE,"E23.0.2.14"),sQuery(id+"F0.wireOp",EDGE,"E23.0.2.22"),sQuery(id+"F0.wireOp",EDGE,"E23.0.2.26"),sQuery(id+"F0.wireOp",EDGE,"E23.0.2.42"),sQuery(id+"F0.wireOp",EDGE,"E23.0.2.44"),sQuery(id+"F0.wireOp",EDGE,"E23.0.2.45"),sQuery(id+"F0.wireOp",EDGE,"E23.0.2.47")])],"isStart":true});
            var Q10;
            Q10=makeQuery(id+"F4.opExtrude","CAP_FACE",FACE,{"disambiguationData":[OSD([sQuery(id+"F0.wireOp",EDGE,"E23.0.2.7"),sQuery(id+"F0.wireOp",EDGE,"E23.0.2.11"),sQuery(id+"F0.wireOp",EDGE,"E23.0.2.16"),sQuery(id+"F0.wireOp",EDGE,"E23.0.2.19"),sQuery(id+"F0.wireOp",EDGE,"E23.0.2.34"),sQuery(id+"F0.wireOp",EDGE,"E23.0.2.37"),sQuery(id+"F0.wireOp",EDGE,"E23.0.2.43"),sQuery(id+"F0.wireOp",EDGE,"E23.0.2.46")])],"isStart":true});
            var Q11;
            Q11=makeQuery(id+"F4.opExtrude","CAP_FACE",FACE,{"disambiguationData":[OSD([sQuery(id+"F0.wireOp",EDGE,"E23.0.2.4"),sQuery(id+"F0.wireOp",EDGE,"E23.0.2.8"),sQuery(id+"F0.wireOp",EDGE,"E23.0.2.17"),sQuery(id+"F0.wireOp",EDGE,"E23.0.2.30"),sQuery(id+"F0.wireOp",EDGE,"E23.0.2.35"),sQuery(id+"F0.wireOp",EDGE,"E23.0.2.38"),sQuery(id+"F0.wireOp",EDGE,"E23.0.2.40"),sQuery(id+"F0.wireOp",EDGE,"E23.0.2.49")])],"isStart":true});
            var Q12;
            Q12=makeQuery(id+"F4.opExtrude","CAP_FACE",FACE,{"disambiguationData":[OSD([sQuery(id+"F0.wireOp",EDGE,"E23.0.1.4"),sQuery(id+"F0.wireOp",EDGE,"E23.0.1.8"),sQuery(id+"F0.wireOp",EDGE,"E23.0.1.17"),sQuery(id+"F0.wireOp",EDGE,"E23.0.1.30"),sQuery(id+"F0.wireOp",EDGE,"E23.0.1.35"),sQuery(id+"F0.wireOp",EDGE,"E23.0.1.38"),sQuery(id+"F0.wireOp",EDGE,"E23.0.1.40"),sQuery(id+"F0.wireOp",EDGE,"E23.0.1.49")])],"isStart":true});
            var Q13;
            Q13=makeQuery(id+"F4.opExtrude","CAP_FACE",FACE,{"disambiguationData":[OSD([sQuery(id+"F0.wireOp",EDGE,"E23.0.1.7"),sQuery(id+"F0.wireOp",EDGE,"E23.0.1.11"),sQuery(id+"F0.wireOp",EDGE,"E23.0.1.16"),sQuery(id+"F0.wireOp",EDGE,"E23.0.1.19"),sQuery(id+"F0.wireOp",EDGE,"E23.0.1.34"),sQuery(id+"F0.wireOp",EDGE,"E23.0.1.37"),sQuery(id+"F0.wireOp",EDGE,"E23.0.1.43"),sQuery(id+"F0.wireOp",EDGE,"E23.0.1.46")])],"isStart":true});
            var Q14;
            Q14=makeQuery(id+"F4.opExtrude","CAP_FACE",FACE,{"disambiguationData":[OSD([sQuery(id+"F0.wireOp",EDGE,"E23.0.1.13"),sQuery(id+"F0.wireOp",EDGE,"E23.0.1.14"),sQuery(id+"F0.wireOp",EDGE,"E23.0.1.22"),sQuery(id+"F0.wireOp",EDGE,"E23.0.1.26"),sQuery(id+"F0.wireOp",EDGE,"E23.0.1.42"),sQuery(id+"F0.wireOp",EDGE,"E23.0.1.44"),sQuery(id+"F0.wireOp",EDGE,"E23.0.1.45"),sQuery(id+"F0.wireOp",EDGE,"E23.0.1.47")])],"isStart":true});
            var Q15;
            Q15=makeQuery(id+"F4.opExtrude","CAP_FACE",FACE,{"disambiguationData":[OSD([sQuery(id+"F0.wireOp",EDGE,"E23.0.1.12"),sQuery(id+"F0.wireOp",EDGE,"E23.0.1.15"),sQuery(id+"F0.wireOp",EDGE,"E23.0.1.28"),sQuery(id+"F0.wireOp",EDGE,"E23.0.1.33"),sQuery(id+"F0.wireOp",EDGE,"E23.0.1.36"),sQuery(id+"F0.wireOp",EDGE,"E23.0.1.39"),sQuery(id+"F0.wireOp",EDGE,"E23.0.1.41"),sQuery(id+"F0.wireOp",EDGE,"E23.0.1.48")])],"isStart":true});
            var Q16;
            Q16=makeQuery(id+"F4.opExtrude","CAP_FACE",FACE,{"disambiguationData":[OSD([sQuery(id+"F0.wireOp",EDGE,"E24.0.1.3"),sQuery(id+"F0.wireOp",EDGE,"E24.0.1.11"),sQuery(id+"F0.wireOp",EDGE,"E24.0.1.26"),sQuery(id+"F0.wireOp",EDGE,"E24.0.1.32"),sQuery(id+"F0.wireOp",EDGE,"E24.0.1.35"),sQuery(id+"F0.wireOp",EDGE,"E24.0.1.42"),sQuery(id+"F0.wireOp",EDGE,"E24.0.1.44"),sQuery(id+"F0.wireOp",EDGE,"E24.0.1.50")])],"isStart":true});
            var Q17;
            Q17=makeQuery(id+"F4.opExtrude","CAP_FACE",FACE,{"disambiguationData":[OSD([sQuery(id+"F0.wireOp",EDGE,"E24.0.1.1"),sQuery(id+"F0.wireOp",EDGE,"E24.0.1.6"),sQuery(id+"F0.wireOp",EDGE,"E24.0.1.17"),sQuery(id+"F0.wireOp",EDGE,"E24.0.1.18"),sQuery(id+"F0.wireOp",EDGE,"E24.0.1.40"),sQuery(id+"F0.wireOp",EDGE,"E24.0.1.43"),sQuery(id+"F0.wireOp",EDGE,"E24.0.1.47"),sQuery(id+"F0.wireOp",EDGE,"E24.0.1.48")])],"isStart":true});
            var Q18;
            Q18=makeQuery(id+"F4.opExtrude","CAP_FACE",FACE,{"disambiguationData":[OSD([sQuery(id+"F0.wireOp",EDGE,"E24.0.1.0"),sQuery(id+"F0.wireOp",EDGE,"E24.0.1.24"),sQuery(id+"F0.wireOp",EDGE,"E24.0.1.25"),sQuery(id+"F0.wireOp",EDGE,"E24.0.1.27"),sQuery(id+"F0.wireOp",EDGE,"E24.0.1.37"),sQuery(id+"F0.wireOp",EDGE,"E24.0.1.38"),sQuery(id+"F0.wireOp",EDGE,"E24.0.1.41"),sQuery(id+"F0.wireOp",EDGE,"E24.0.1.49")])],"isStart":true});
            var Q19;
            Q19=makeQuery(id+"F4.opExtrude","CAP_FACE",FACE,{"disambiguationData":[OSD([sQuery(id+"F0.wireOp",EDGE,"E24.0.1.16"),sQuery(id+"F0.wireOp",EDGE,"E24.0.1.28"),sQuery(id+"F0.wireOp",EDGE,"E24.0.1.31"),sQuery(id+"F0.wireOp",EDGE,"E24.0.1.33"),sQuery(id+"F0.wireOp",EDGE,"E24.0.1.36"),sQuery(id+"F0.wireOp",EDGE,"E24.0.1.39"),sQuery(id+"F0.wireOp",EDGE,"E24.0.1.45"),sQuery(id+"F0.wireOp",EDGE,"E24.0.1.46")])],"isStart":true});
            var Q20;
            Q20=makeQuery(id+"F4.opExtrude","CAP_FACE",FACE,{"disambiguationData":[OSD([sQuery(id+"F0.wireOp",EDGE,"E24.0.2.16"),sQuery(id+"F0.wireOp",EDGE,"E24.0.2.28"),sQuery(id+"F0.wireOp",EDGE,"E24.0.2.31"),sQuery(id+"F0.wireOp",EDGE,"E24.0.2.33"),sQuery(id+"F0.wireOp",EDGE,"E24.0.2.36"),sQuery(id+"F0.wireOp",EDGE,"E24.0.2.39"),sQuery(id+"F0.wireOp",EDGE,"E24.0.2.45"),sQuery(id+"F0.wireOp",EDGE,"E24.0.2.46")])],"isStart":true});
            var Q21;
            Q21=makeQuery(id+"F4.opExtrude","CAP_FACE",FACE,{"disambiguationData":[OSD([sQuery(id+"F0.wireOp",EDGE,"E24.0.2.0"),sQuery(id+"F0.wireOp",EDGE,"E24.0.2.24"),sQuery(id+"F0.wireOp",EDGE,"E24.0.2.25"),sQuery(id+"F0.wireOp",EDGE,"E24.0.2.27"),sQuery(id+"F0.wireOp",EDGE,"E24.0.2.37"),sQuery(id+"F0.wireOp",EDGE,"E24.0.2.38"),sQuery(id+"F0.wireOp",EDGE,"E24.0.2.41"),sQuery(id+"F0.wireOp",EDGE,"E24.0.2.49")])],"isStart":true});
            var Q22;
            Q22=makeQuery(id+"F4.opExtrude","CAP_FACE",FACE,{"disambiguationData":[OSD([sQuery(id+"F0.wireOp",EDGE,"E24.0.2.1"),sQuery(id+"F0.wireOp",EDGE,"E24.0.2.6"),sQuery(id+"F0.wireOp",EDGE,"E24.0.2.17"),sQuery(id+"F0.wireOp",EDGE,"E24.0.2.18"),sQuery(id+"F0.wireOp",EDGE,"E24.0.2.40"),sQuery(id+"F0.wireOp",EDGE,"E24.0.2.43"),sQuery(id+"F0.wireOp",EDGE,"E24.0.2.47"),sQuery(id+"F0.wireOp",EDGE,"E24.0.2.48")])],"isStart":true});
            var Q23;
            Q23=makeQuery(id+"F4.opExtrude","CAP_FACE",FACE,{"disambiguationData":[OSD([sQuery(id+"F0.wireOp",EDGE,"E24.0.2.3"),sQuery(id+"F0.wireOp",EDGE,"E24.0.2.11"),sQuery(id+"F0.wireOp",EDGE,"E24.0.2.26"),sQuery(id+"F0.wireOp",EDGE,"E24.0.2.32"),sQuery(id+"F0.wireOp",EDGE,"E24.0.2.35"),sQuery(id+"F0.wireOp",EDGE,"E24.0.2.42"),sQuery(id+"F0.wireOp",EDGE,"E24.0.2.44"),sQuery(id+"F0.wireOp",EDGE,"E24.0.2.50")])],"isStart":true});
            var Q24;
            Q24=makeQuery(id+"F4.opExtrude","CAP_FACE",FACE,{"disambiguationData":[OSD([sQuery(id+"F0.wireOp",EDGE,"E24.0.3.3"),sQuery(id+"F0.wireOp",EDGE,"E24.0.3.11"),sQuery(id+"F0.wireOp",EDGE,"E24.0.3.26"),sQuery(id+"F0.wireOp",EDGE,"E24.0.3.32"),sQuery(id+"F0.wireOp",EDGE,"E24.0.3.35"),sQuery(id+"F0.wireOp",EDGE,"E24.0.3.42"),sQuery(id+"F0.wireOp",EDGE,"E24.0.3.44"),sQuery(id+"F0.wireOp",EDGE,"E24.0.3.50")])],"isStart":true});
            var Q25;
            Q25=makeQuery(id+"F4.opExtrude","CAP_FACE",FACE,{"disambiguationData":[OSD([sQuery(id+"F0.wireOp",EDGE,"E24.0.3.1"),sQuery(id+"F0.wireOp",EDGE,"E24.0.3.6"),sQuery(id+"F0.wireOp",EDGE,"E24.0.3.17"),sQuery(id+"F0.wireOp",EDGE,"E24.0.3.18"),sQuery(id+"F0.wireOp",EDGE,"E24.0.3.40"),sQuery(id+"F0.wireOp",EDGE,"E24.0.3.43"),sQuery(id+"F0.wireOp",EDGE,"E24.0.3.47"),sQuery(id+"F0.wireOp",EDGE,"E24.0.3.48")])],"isStart":true});
            var Q26;
            Q26=makeQuery(id+"F4.opExtrude","CAP_FACE",FACE,{"disambiguationData":[OSD([sQuery(id+"F0.wireOp",EDGE,"E24.0.3.0"),sQuery(id+"F0.wireOp",EDGE,"E24.0.3.24"),sQuery(id+"F0.wireOp",EDGE,"E24.0.3.25"),sQuery(id+"F0.wireOp",EDGE,"E24.0.3.27"),sQuery(id+"F0.wireOp",EDGE,"E24.0.3.37"),sQuery(id+"F0.wireOp",EDGE,"E24.0.3.38"),sQuery(id+"F0.wireOp",EDGE,"E24.0.3.41"),sQuery(id+"F0.wireOp",EDGE,"E24.0.3.49")])],"isStart":true});
            var Q27;
            Q27=makeQuery(id+"F4.opExtrude","CAP_FACE",FACE,{"disambiguationData":[OSD([sQuery(id+"F0.wireOp",EDGE,"E24.0.3.16"),sQuery(id+"F0.wireOp",EDGE,"E24.0.3.28"),sQuery(id+"F0.wireOp",EDGE,"E24.0.3.31"),sQuery(id+"F0.wireOp",EDGE,"E24.0.3.33"),sQuery(id+"F0.wireOp",EDGE,"E24.0.3.36"),sQuery(id+"F0.wireOp",EDGE,"E24.0.3.39"),sQuery(id+"F0.wireOp",EDGE,"E24.0.3.45"),sQuery(id+"F0.wireOp",EDGE,"E24.0.3.46")])],"isStart":true});
            shell(context, id + "F5", {"entities" : qUnion([Q0, Q1, Q2, Q3, Q4, Q5, Q6, Q7, Q8, Q9, Q10, Q11, Q12, Q13, Q14, Q15, Q16, Q17, Q18, Q19, Q20, Q21, Q22, Q23, Q24, Q25, Q26, Q27]), "thickness" : .5 * mm});
        }
        {
            var Q0;
            Q0=makeQuery(id+"F2.opExtrude","SWEPT_EDGE",EDGE,{"disambiguationData":[OSD([sQuery(id+"F1.wireOp",EDGE,"E25.top"),sQuery(id+"F1.wireOp",EDGE,"E25.left")])]});
            var Q1;
            Q1=makeQuery(id+"F2.opExtrude","SWEPT_EDGE",EDGE,{"disambiguationData":[OSD([sQuery(id+"F1.wireOp",EDGE,"E25.top"),sQuery(id+"F1.wireOp",EDGE,"E25.right")])]});
            var Q2;
            Q2=makeQuery(id+"F2.opExtrude","SWEPT_EDGE",EDGE,{"disambiguationData":[OSD([sQuery(id+"F1.wireOp",EDGE,"E25.bottom"),sQuery(id+"F1.wireOp",EDGE,"E25.right")])]});
            var Q3;
            Q3=makeQuery(id+"F2.opExtrude","SWEPT_EDGE",EDGE,{"disambiguationData":[OSD([sQuery(id+"F1.wireOp",EDGE,"E25.bottom"),sQuery(id+"F1.wireOp",EDGE,"E25.left")])]});
            fillet(context, id + "F6", {"entities" : qUnion([Q0, Q1, Q2, Q3]), "radius" : 2 * mm, "tangentPropagation" : true, "allowEdgeOverflow" : false});
        }
        {
            var Q0;
            Q0=makeQuery(id+"F4.opExtrude","CAP_FACE",FACE,{"disambiguationData":[OSD([sQuery(id+"F0.wireOp",EDGE,"E2.bottom"),sQuery(id+"F0.wireOp",EDGE,"E2.top"),sQuery(id+"F0.wireOp",EDGE,"E2.left"),sQuery(id+"F0.wireOp",EDGE,"E2.right"),sQuery(id+"F0.wireOp",EDGE,"E4.filletArc"),sQuery(id+"F0.wireOp",EDGE,"E5.filletArc"),sQuery(id+"F0.wireOp",EDGE,"E6.filletArc"),sQuery(id+"F0.wireOp",EDGE,"E7.filletArc")])],"isStart":false});
            var Q1;
            Q1=makeQuery(id+"F4.opExtrude","CAP_FACE",FACE,{"disambiguationData":[OSD([sQuery(id+"F0.wireOp",EDGE,"E8.bottom"),sQuery(id+"F0.wireOp",EDGE,"E8.top"),sQuery(id+"F0.wireOp",EDGE,"E8.left"),sQuery(id+"F0.wireOp",EDGE,"E8.right"),sQuery(id+"F0.wireOp",EDGE,"E11.filletArc"),sQuery(id+"F0.wireOp",EDGE,"E12.filletArc"),sQuery(id+"F0.wireOp",EDGE,"E13.filletArc"),sQuery(id+"F0.wireOp",EDGE,"E14.filletArc")])],"isStart":false});
            var Q2;
            Q2=makeQuery(id+"F4.opExtrude","CAP_FACE",FACE,{"disambiguationData":[OSD([sQuery(id+"F0.wireOp",EDGE,"E9.bottom"),sQuery(id+"F0.wireOp",EDGE,"E9.top"),sQuery(id+"F0.wireOp",EDGE,"E9.left"),sQuery(id+"F0.wireOp",EDGE,"E9.right"),sQuery(id+"F0.wireOp",EDGE,"E15.filletArc"),sQuery(id+"F0.wireOp",EDGE,"E16.filletArc"),sQuery(id+"F0.wireOp",EDGE,"E17.filletArc"),sQuery(id+"F0.wireOp",EDGE,"E18.filletArc")])],"isStart":false});
            var Q3;
            Q3=makeQuery(id+"F4.opExtrude","CAP_FACE",FACE,{"disambiguationData":[OSD([sQuery(id+"F0.wireOp",EDGE,"E10.bottom"),sQuery(id+"F0.wireOp",EDGE,"E10.top"),sQuery(id+"F0.wireOp",EDGE,"E10.left"),sQuery(id+"F0.wireOp",EDGE,"E10.right"),sQuery(id+"F0.wireOp",EDGE,"E19.filletArc"),sQuery(id+"F0.wireOp",EDGE,"E20.filletArc"),sQuery(id+"F0.wireOp",EDGE,"E21.filletArc"),sQuery(id+"F0.wireOp",EDGE,"E22.filletArc")])],"isStart":false});
            var Q4;
            Q4=makeQuery(id+"F4.opExtrude","CAP_FACE",FACE,{"disambiguationData":[OSD([sQuery(id+"F0.wireOp",EDGE,"E24.0.3.16"),sQuery(id+"F0.wireOp",EDGE,"E24.0.3.28"),sQuery(id+"F0.wireOp",EDGE,"E24.0.3.31"),sQuery(id+"F0.wireOp",EDGE,"E24.0.3.33"),sQuery(id+"F0.wireOp",EDGE,"E24.0.3.36"),sQuery(id+"F0.wireOp",EDGE,"E24.0.3.39"),sQuery(id+"F0.wireOp",EDGE,"E24.0.3.45"),sQuery(id+"F0.wireOp",EDGE,"E24.0.3.46")])],"isStart":false});
            var Q5;
            Q5=makeQuery(id+"F4.opExtrude","CAP_FACE",FACE,{"disambiguationData":[OSD([sQuery(id+"F0.wireOp",EDGE,"E24.0.3.0"),sQuery(id+"F0.wireOp",EDGE,"E24.0.3.24"),sQuery(id+"F0.wireOp",EDGE,"E24.0.3.25"),sQuery(id+"F0.wireOp",EDGE,"E24.0.3.27"),sQuery(id+"F0.wireOp",EDGE,"E24.0.3.37"),sQuery(id+"F0.wireOp",EDGE,"E24.0.3.38"),sQuery(id+"F0.wireOp",EDGE,"E24.0.3.41"),sQuery(id+"F0.wireOp",EDGE,"E24.0.3.49")])],"isStart":false});
            var Q6;
            Q6=makeQuery(id+"F4.opExtrude","CAP_FACE",FACE,{"disambiguationData":[OSD([sQuery(id+"F0.wireOp",EDGE,"E24.0.3.1"),sQuery(id+"F0.wireOp",EDGE,"E24.0.3.6"),sQuery(id+"F0.wireOp",EDGE,"E24.0.3.17"),sQuery(id+"F0.wireOp",EDGE,"E24.0.3.18"),sQuery(id+"F0.wireOp",EDGE,"E24.0.3.40"),sQuery(id+"F0.wireOp",EDGE,"E24.0.3.43"),sQuery(id+"F0.wireOp",EDGE,"E24.0.3.47"),sQuery(id+"F0.wireOp",EDGE,"E24.0.3.48")])],"isStart":false});
            var Q7;
            Q7=makeQuery(id+"F4.opExtrude","CAP_FACE",FACE,{"disambiguationData":[OSD([sQuery(id+"F0.wireOp",EDGE,"E24.0.3.3"),sQuery(id+"F0.wireOp",EDGE,"E24.0.3.11"),sQuery(id+"F0.wireOp",EDGE,"E24.0.3.26"),sQuery(id+"F0.wireOp",EDGE,"E24.0.3.32"),sQuery(id+"F0.wireOp",EDGE,"E24.0.3.35"),sQuery(id+"F0.wireOp",EDGE,"E24.0.3.42"),sQuery(id+"F0.wireOp",EDGE,"E24.0.3.44"),sQuery(id+"F0.wireOp",EDGE,"E24.0.3.50")])],"isStart":false});
            var Q8;
            Q8=makeQuery(id+"F4.opExtrude","CAP_FACE",FACE,{"disambiguationData":[OSD([sQuery(id+"F0.wireOp",EDGE,"E24.0.2.16"),sQuery(id+"F0.wireOp",EDGE,"E24.0.2.28"),sQuery(id+"F0.wireOp",EDGE,"E24.0.2.31"),sQuery(id+"F0.wireOp",EDGE,"E24.0.2.33"),sQuery(id+"F0.wireOp",EDGE,"E24.0.2.36"),sQuery(id+"F0.wireOp",EDGE,"E24.0.2.39"),sQuery(id+"F0.wireOp",EDGE,"E24.0.2.45"),sQuery(id+"F0.wireOp",EDGE,"E24.0.2.46")])],"isStart":false});
            var Q9;
            Q9=makeQuery(id+"F4.opExtrude","CAP_FACE",FACE,{"disambiguationData":[OSD([sQuery(id+"F0.wireOp",EDGE,"E24.0.2.0"),sQuery(id+"F0.wireOp",EDGE,"E24.0.2.24"),sQuery(id+"F0.wireOp",EDGE,"E24.0.2.25"),sQuery(id+"F0.wireOp",EDGE,"E24.0.2.27"),sQuery(id+"F0.wireOp",EDGE,"E24.0.2.37"),sQuery(id+"F0.wireOp",EDGE,"E24.0.2.38"),sQuery(id+"F0.wireOp",EDGE,"E24.0.2.41"),sQuery(id+"F0.wireOp",EDGE,"E24.0.2.49")])],"isStart":false});
            var Q10;
            Q10=makeQuery(id+"F4.opExtrude","CAP_FACE",FACE,{"disambiguationData":[OSD([sQuery(id+"F0.wireOp",EDGE,"E24.0.2.1"),sQuery(id+"F0.wireOp",EDGE,"E24.0.2.6"),sQuery(id+"F0.wireOp",EDGE,"E24.0.2.17"),sQuery(id+"F0.wireOp",EDGE,"E24.0.2.18"),sQuery(id+"F0.wireOp",EDGE,"E24.0.2.40"),sQuery(id+"F0.wireOp",EDGE,"E24.0.2.43"),sQuery(id+"F0.wireOp",EDGE,"E24.0.2.47"),sQuery(id+"F0.wireOp",EDGE,"E24.0.2.48")])],"isStart":false});
            var Q11;
            Q11=makeQuery(id+"F4.opExtrude","CAP_FACE",FACE,{"disambiguationData":[OSD([sQuery(id+"F0.wireOp",EDGE,"E24.0.2.3"),sQuery(id+"F0.wireOp",EDGE,"E24.0.2.11"),sQuery(id+"F0.wireOp",EDGE,"E24.0.2.26"),sQuery(id+"F0.wireOp",EDGE,"E24.0.2.32"),sQuery(id+"F0.wireOp",EDGE,"E24.0.2.35"),sQuery(id+"F0.wireOp",EDGE,"E24.0.2.42"),sQuery(id+"F0.wireOp",EDGE,"E24.0.2.44"),sQuery(id+"F0.wireOp",EDGE,"E24.0.2.50")])],"isStart":false});
            var Q12;
            Q12=makeQuery(id+"F4.opExtrude","CAP_FACE",FACE,{"disambiguationData":[OSD([sQuery(id+"F0.wireOp",EDGE,"E24.0.1.3"),sQuery(id+"F0.wireOp",EDGE,"E24.0.1.11"),sQuery(id+"F0.wireOp",EDGE,"E24.0.1.26"),sQuery(id+"F0.wireOp",EDGE,"E24.0.1.32"),sQuery(id+"F0.wireOp",EDGE,"E24.0.1.35"),sQuery(id+"F0.wireOp",EDGE,"E24.0.1.42"),sQuery(id+"F0.wireOp",EDGE,"E24.0.1.44"),sQuery(id+"F0.wireOp",EDGE,"E24.0.1.50")])],"isStart":false});
            var Q13;
            Q13=makeQuery(id+"F4.opExtrude","CAP_FACE",FACE,{"disambiguationData":[OSD([sQuery(id+"F0.wireOp",EDGE,"E24.0.1.1"),sQuery(id+"F0.wireOp",EDGE,"E24.0.1.6"),sQuery(id+"F0.wireOp",EDGE,"E24.0.1.17"),sQuery(id+"F0.wireOp",EDGE,"E24.0.1.18"),sQuery(id+"F0.wireOp",EDGE,"E24.0.1.40"),sQuery(id+"F0.wireOp",EDGE,"E24.0.1.43"),sQuery(id+"F0.wireOp",EDGE,"E24.0.1.47"),sQuery(id+"F0.wireOp",EDGE,"E24.0.1.48")])],"isStart":false});
            var Q14;
            Q14=makeQuery(id+"F4.opExtrude","CAP_FACE",FACE,{"disambiguationData":[OSD([sQuery(id+"F0.wireOp",EDGE,"E24.0.1.0"),sQuery(id+"F0.wireOp",EDGE,"E24.0.1.24"),sQuery(id+"F0.wireOp",EDGE,"E24.0.1.25"),sQuery(id+"F0.wireOp",EDGE,"E24.0.1.27"),sQuery(id+"F0.wireOp",EDGE,"E24.0.1.37"),sQuery(id+"F0.wireOp",EDGE,"E24.0.1.38"),sQuery(id+"F0.wireOp",EDGE,"E24.0.1.41"),sQuery(id+"F0.wireOp",EDGE,"E24.0.1.49")])],"isStart":false});
            var Q15;
            Q15=makeQuery(id+"F4.opExtrude","CAP_FACE",FACE,{"disambiguationData":[OSD([sQuery(id+"F0.wireOp",EDGE,"E24.0.1.16"),sQuery(id+"F0.wireOp",EDGE,"E24.0.1.28"),sQuery(id+"F0.wireOp",EDGE,"E24.0.1.31"),sQuery(id+"F0.wireOp",EDGE,"E24.0.1.33"),sQuery(id+"F0.wireOp",EDGE,"E24.0.1.36"),sQuery(id+"F0.wireOp",EDGE,"E24.0.1.39"),sQuery(id+"F0.wireOp",EDGE,"E24.0.1.45"),sQuery(id+"F0.wireOp",EDGE,"E24.0.1.46")])],"isStart":false});
            var Q16;
            Q16=makeQuery(id+"F4.opExtrude","CAP_FACE",FACE,{"disambiguationData":[OSD([sQuery(id+"F0.wireOp",EDGE,"E23.0.1.4"),sQuery(id+"F0.wireOp",EDGE,"E23.0.1.8"),sQuery(id+"F0.wireOp",EDGE,"E23.0.1.17"),sQuery(id+"F0.wireOp",EDGE,"E23.0.1.30"),sQuery(id+"F0.wireOp",EDGE,"E23.0.1.35"),sQuery(id+"F0.wireOp",EDGE,"E23.0.1.38"),sQuery(id+"F0.wireOp",EDGE,"E23.0.1.40"),sQuery(id+"F0.wireOp",EDGE,"E23.0.1.49")])],"isStart":false});
            var Q17;
            Q17=makeQuery(id+"F4.opExtrude","CAP_FACE",FACE,{"disambiguationData":[OSD([sQuery(id+"F0.wireOp",EDGE,"E23.0.1.7"),sQuery(id+"F0.wireOp",EDGE,"E23.0.1.11"),sQuery(id+"F0.wireOp",EDGE,"E23.0.1.16"),sQuery(id+"F0.wireOp",EDGE,"E23.0.1.19"),sQuery(id+"F0.wireOp",EDGE,"E23.0.1.34"),sQuery(id+"F0.wireOp",EDGE,"E23.0.1.37"),sQuery(id+"F0.wireOp",EDGE,"E23.0.1.43"),sQuery(id+"F0.wireOp",EDGE,"E23.0.1.46")])],"isStart":false});
            var Q18;
            Q18=makeQuery(id+"F4.opExtrude","CAP_FACE",FACE,{"disambiguationData":[OSD([sQuery(id+"F0.wireOp",EDGE,"E23.0.1.13"),sQuery(id+"F0.wireOp",EDGE,"E23.0.1.14"),sQuery(id+"F0.wireOp",EDGE,"E23.0.1.22"),sQuery(id+"F0.wireOp",EDGE,"E23.0.1.26"),sQuery(id+"F0.wireOp",EDGE,"E23.0.1.42"),sQuery(id+"F0.wireOp",EDGE,"E23.0.1.44"),sQuery(id+"F0.wireOp",EDGE,"E23.0.1.45"),sQuery(id+"F0.wireOp",EDGE,"E23.0.1.47")])],"isStart":false});
            var Q19;
            Q19=makeQuery(id+"F4.opExtrude","CAP_FACE",FACE,{"disambiguationData":[OSD([sQuery(id+"F0.wireOp",EDGE,"E23.0.1.12"),sQuery(id+"F0.wireOp",EDGE,"E23.0.1.15"),sQuery(id+"F0.wireOp",EDGE,"E23.0.1.28"),sQuery(id+"F0.wireOp",EDGE,"E23.0.1.33"),sQuery(id+"F0.wireOp",EDGE,"E23.0.1.36"),sQuery(id+"F0.wireOp",EDGE,"E23.0.1.39"),sQuery(id+"F0.wireOp",EDGE,"E23.0.1.41"),sQuery(id+"F0.wireOp",EDGE,"E23.0.1.48")])],"isStart":false});
            var Q20;
            Q20=makeQuery(id+"F4.opExtrude","CAP_FACE",FACE,{"disambiguationData":[OSD([sQuery(id+"F0.wireOp",EDGE,"E23.0.2.12"),sQuery(id+"F0.wireOp",EDGE,"E23.0.2.15"),sQuery(id+"F0.wireOp",EDGE,"E23.0.2.28"),sQuery(id+"F0.wireOp",EDGE,"E23.0.2.33"),sQuery(id+"F0.wireOp",EDGE,"E23.0.2.36"),sQuery(id+"F0.wireOp",EDGE,"E23.0.2.39"),sQuery(id+"F0.wireOp",EDGE,"E23.0.2.41"),sQuery(id+"F0.wireOp",EDGE,"E23.0.2.48")])],"isStart":false});
            var Q21;
            Q21=makeQuery(id+"F4.opExtrude","CAP_FACE",FACE,{"disambiguationData":[OSD([sQuery(id+"F0.wireOp",EDGE,"E23.0.2.13"),sQuery(id+"F0.wireOp",EDGE,"E23.0.2.14"),sQuery(id+"F0.wireOp",EDGE,"E23.0.2.22"),sQuery(id+"F0.wireOp",EDGE,"E23.0.2.26"),sQuery(id+"F0.wireOp",EDGE,"E23.0.2.42"),sQuery(id+"F0.wireOp",EDGE,"E23.0.2.44"),sQuery(id+"F0.wireOp",EDGE,"E23.0.2.45"),sQuery(id+"F0.wireOp",EDGE,"E23.0.2.47")])],"isStart":false});
            var Q22;
            Q22=makeQuery(id+"F4.opExtrude","CAP_FACE",FACE,{"disambiguationData":[OSD([sQuery(id+"F0.wireOp",EDGE,"E23.0.2.7"),sQuery(id+"F0.wireOp",EDGE,"E23.0.2.11"),sQuery(id+"F0.wireOp",EDGE,"E23.0.2.16"),sQuery(id+"F0.wireOp",EDGE,"E23.0.2.19"),sQuery(id+"F0.wireOp",EDGE,"E23.0.2.34"),sQuery(id+"F0.wireOp",EDGE,"E23.0.2.37"),sQuery(id+"F0.wireOp",EDGE,"E23.0.2.43"),sQuery(id+"F0.wireOp",EDGE,"E23.0.2.46")])],"isStart":false});
            var Q23;
            Q23=makeQuery(id+"F4.opExtrude","CAP_FACE",FACE,{"disambiguationData":[OSD([sQuery(id+"F0.wireOp",EDGE,"E23.0.2.4"),sQuery(id+"F0.wireOp",EDGE,"E23.0.2.8"),sQuery(id+"F0.wireOp",EDGE,"E23.0.2.17"),sQuery(id+"F0.wireOp",EDGE,"E23.0.2.30"),sQuery(id+"F0.wireOp",EDGE,"E23.0.2.35"),sQuery(id+"F0.wireOp",EDGE,"E23.0.2.38"),sQuery(id+"F0.wireOp",EDGE,"E23.0.2.40"),sQuery(id+"F0.wireOp",EDGE,"E23.0.2.49")])],"isStart":false});
            var Q24;
            Q24=makeQuery(id+"F4.opExtrude","CAP_FACE",FACE,{"disambiguationData":[OSD([sQuery(id+"F0.wireOp",EDGE,"E23.0.3.4"),sQuery(id+"F0.wireOp",EDGE,"E23.0.3.8"),sQuery(id+"F0.wireOp",EDGE,"E23.0.3.17"),sQuery(id+"F0.wireOp",EDGE,"E23.0.3.30"),sQuery(id+"F0.wireOp",EDGE,"E23.0.3.35"),sQuery(id+"F0.wireOp",EDGE,"E23.0.3.38"),sQuery(id+"F0.wireOp",EDGE,"E23.0.3.40"),sQuery(id+"F0.wireOp",EDGE,"E23.0.3.49")])],"isStart":false});
            var Q25;
            Q25=makeQuery(id+"F4.opExtrude","CAP_FACE",FACE,{"disambiguationData":[OSD([sQuery(id+"F0.wireOp",EDGE,"E23.0.3.7"),sQuery(id+"F0.wireOp",EDGE,"E23.0.3.11"),sQuery(id+"F0.wireOp",EDGE,"E23.0.3.16"),sQuery(id+"F0.wireOp",EDGE,"E23.0.3.19"),sQuery(id+"F0.wireOp",EDGE,"E23.0.3.34"),sQuery(id+"F0.wireOp",EDGE,"E23.0.3.37"),sQuery(id+"F0.wireOp",EDGE,"E23.0.3.43"),sQuery(id+"F0.wireOp",EDGE,"E23.0.3.46")])],"isStart":false});
            var Q26;
            Q26=makeQuery(id+"F4.opExtrude","CAP_FACE",FACE,{"disambiguationData":[OSD([sQuery(id+"F0.wireOp",EDGE,"E23.0.3.13"),sQuery(id+"F0.wireOp",EDGE,"E23.0.3.14"),sQuery(id+"F0.wireOp",EDGE,"E23.0.3.22"),sQuery(id+"F0.wireOp",EDGE,"E23.0.3.26"),sQuery(id+"F0.wireOp",EDGE,"E23.0.3.42"),sQuery(id+"F0.wireOp",EDGE,"E23.0.3.44"),sQuery(id+"F0.wireOp",EDGE,"E23.0.3.45"),sQuery(id+"F0.wireOp",EDGE,"E23.0.3.47")])],"isStart":false});
            var Q27;
            Q27=makeQuery(id+"F4.opExtrude","CAP_FACE",FACE,{"disambiguationData":[OSD([sQuery(id+"F0.wireOp",EDGE,"E23.0.3.12"),sQuery(id+"F0.wireOp",EDGE,"E23.0.3.15"),sQuery(id+"F0.wireOp",EDGE,"E23.0.3.28"),sQuery(id+"F0.wireOp",EDGE,"E23.0.3.33"),sQuery(id+"F0.wireOp",EDGE,"E23.0.3.36"),sQuery(id+"F0.wireOp",EDGE,"E23.0.3.39"),sQuery(id+"F0.wireOp",EDGE,"E23.0.3.41"),sQuery(id+"F0.wireOp",EDGE,"E23.0.3.48")])],"isStart":false});
            fillet(context, id + "F7", {"entities" : qUnion([Q0, Q1, Q2, Q3, Q4, Q5, Q6, Q7, Q8, Q9, Q10, Q11, Q12, Q13, Q14, Q15, Q16, Q17, Q18, Q19, Q20, Q21, Q22, Q23, Q24, Q25, Q26, Q27]), "radius" : .5 * mm, "tangentPropagation" : true, "allowEdgeOverflow" : false});
        }
    });
